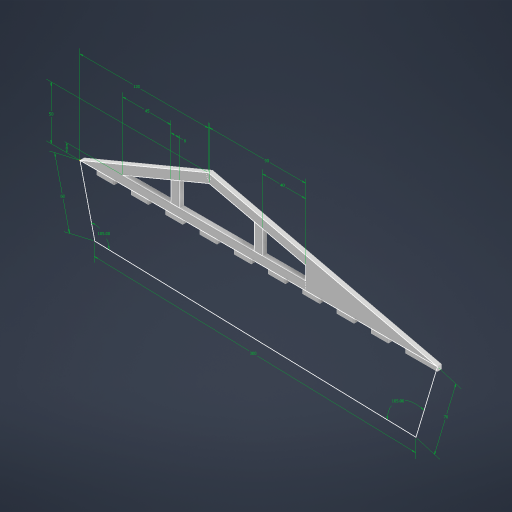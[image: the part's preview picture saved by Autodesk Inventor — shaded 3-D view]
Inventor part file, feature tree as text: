
AUTODESK INVENTOR PART (.ipt)
format: ipt  version: 2023.2 (Build 272271000, 271)  size: 331,264 bytes
history: native  units: mm
features: sketch x2
ambient origin geometry x8: Origin, YZ Plane, XZ Plane, XY Plane, X Axis, Y Axis, Z Axis, Center Point
bodies: Body1 (feature_tree)
feature tree (2):
  sketch  "Sketch1"  dims[d228=105.0deg d268=60.0mm]
  sketch  "Sketch2"  dims[d269=70.0mm d270=300.0mm d273=120.0mm d274=50.0mm d275=105.0deg d283=90.0mm d284=40.0mm d285=45.0mm d286=4.0mm d287=0.0mm d289=8.0mm d290=8.0mm d292=16.0mm d296=16.0mm d297=4.0mm d299=4.0mm d300=0.0mm d9=0.5mm d10=0.872665mm d11=0.5mm d12=0.872665mm d13=0.5mm d14=0.872665mm d27=0.5mm d28=0.872665mm d29=0.5mm d30=0.872665mm d88=0.5mm d89=0.872665mm d90=0.5mm d91=0.872665mm d116=0.5mm d117=0.872665mm d118=0.5mm d119=0.872665mm d154=0.5mm d155=0.872665mm d156=0.5mm d157=0.872665mm d181=0.5mm d182=0.872665mm d183=0.5mm d184=0.872665mm d221=0.5mm d222=0.872665mm d223=0.5mm d224=0.872665mm d301=0.5mm d302=0.872665mm d303=0.5mm d304=0.872665mm]
